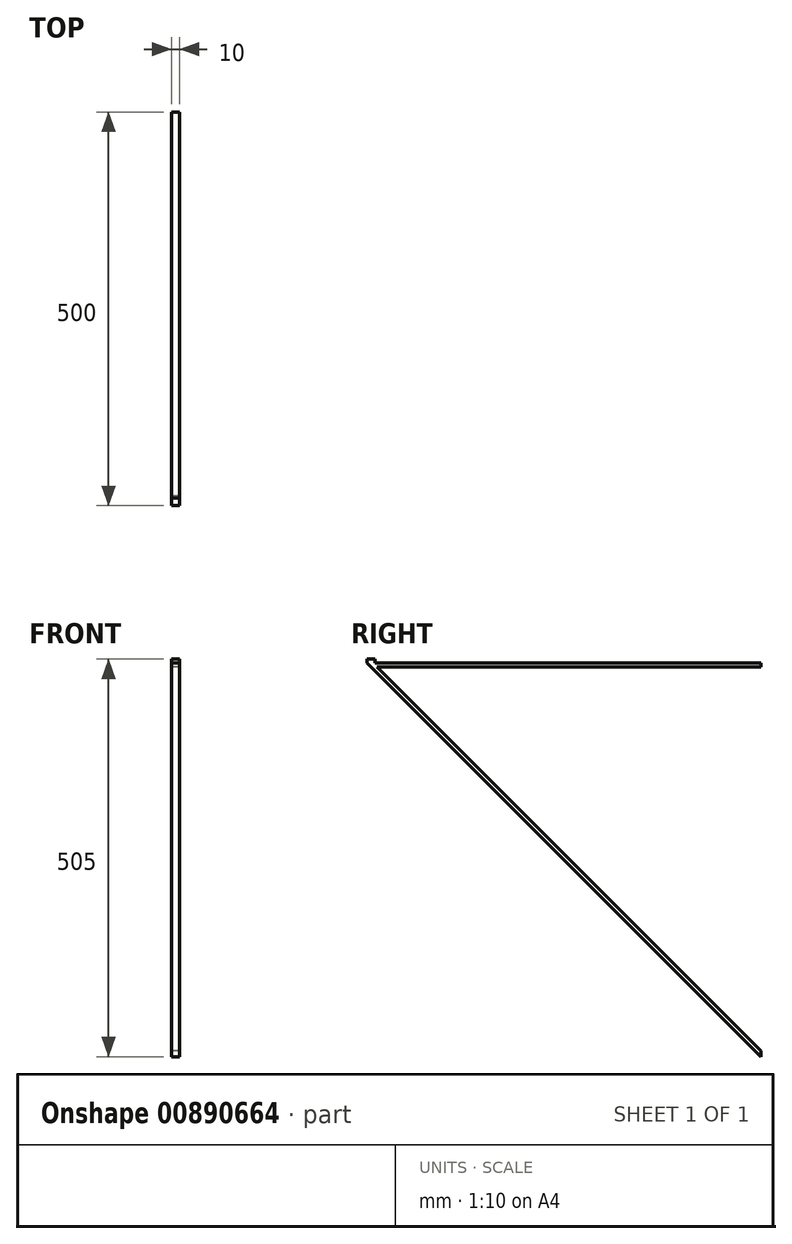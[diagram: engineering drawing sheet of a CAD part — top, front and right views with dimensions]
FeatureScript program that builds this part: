
annotation { "Feature Type Name" : "Feature", "Feature Type Description" : "" }
export const myFeature = defineFeature(function(context is Context, id is Id, definition is map)
    precondition{}
    {
        {
            var Q0;
            Q0=qCreatedBy(makeId("Right.planeOp"),FACE);
            var sketch = newSketch(context, id + "F0", { "sketchPlane" : qUnion([Q0])});
            skLineSegment(sketch, "E0", {"start": v(0, 0) * mm, "end": v(-500, 0) * mm});
            skLineSegment(sketch, "E1", {"start": v(0, 0) * mm, "end": v(0, -500) * mm});
            skLineSegment(sketch, "E2", {"start": v(0, -500) * mm, "end": v(-500, 0) * mm});
            skLineSegment(sketch, "E3", {"start": v(-487.77, -4.92) * mm, "end": v(0, -4.92) * mm});
            skLineSegment(sketch, "E4", {"start": v(-487.77, -4.92) * mm, "end": v(0, -492.69) * mm});
            skSolve(sketch);
        }
        {
            var Q0;
            {var subQ3=sQuery(id+"F0.wireOp",EDGE,"E0");Q0=makeQuery(id+"F0.imprint","IMPRINT",FACE,{"disambiguationData":[TD([[makeQuery(id+"F0.imprint","IMPRINT",EDGE,{"derivedFrom":subQ3}),1.0]])]});}
            extrude(context, id + "F1", {"entities" : qUnion([Q0]), "depth" : 10 * mm, "offsetDistance" : 25 * mm});
        }
        {
            var Q0;
            Q0=makeQuery(id+"F1.opExtrude","SWEPT_FACE",FACE,{"disambiguationData":[OSD([sQuery(id+"F0.wireOp",EDGE,"E0")])]});
            var sketch = newSketch(context, id + "F2", { "sketchPlane" : qUnion([Q0])});
            skLineSegment(sketch, "E5.bottom", {"start": v(0, -500) * mm, "end": v(10, -500) * mm});
            skLineSegment(sketch, "E5.top", {"start": v(0, -500) * mm, "end": v(10, -500) * mm});
            skLineSegment(sketch, "E5.left", {"start": v(0, -500) * mm, "end": v(0, -500) * mm});
            skLineSegment(sketch, "E5.right", {"start": v(10, -500) * mm, "end": v(10, -500) * mm});
            skLineSegment(sketch, "E6.bottom", {"start": v(10, -490) * mm, "end": v(0, -490) * mm});
            skLineSegment(sketch, "E6.top", {"start": v(10, -500) * mm, "end": v(0, -500) * mm});
            skLineSegment(sketch, "E6.left", {"start": v(10, -490) * mm, "end": v(10, -500) * mm});
            skLineSegment(sketch, "E6.right", {"start": v(0, -490) * mm, "end": v(0, -500) * mm});
            skSolve(sketch);
        }
        {
            var Q0;
            Q0=makeQuery(id+"F2.imprint","IMPRINT",FACE,{"disambiguationData":[TD([[makeQuery(id+"F2.imprint","IMPRINT",EDGE,{"derivedFrom":sQuery(id+"F2.wireOp",EDGE,"E6.bottom")}),1.0]])]});
            extrude(context, id + "F3", {"entities" : qUnion([Q0]), "operationType" : NewBodyOperationType.ADD, "depth" : 5 * mm, "offsetDistance" : 25 * mm});
        }
    });
